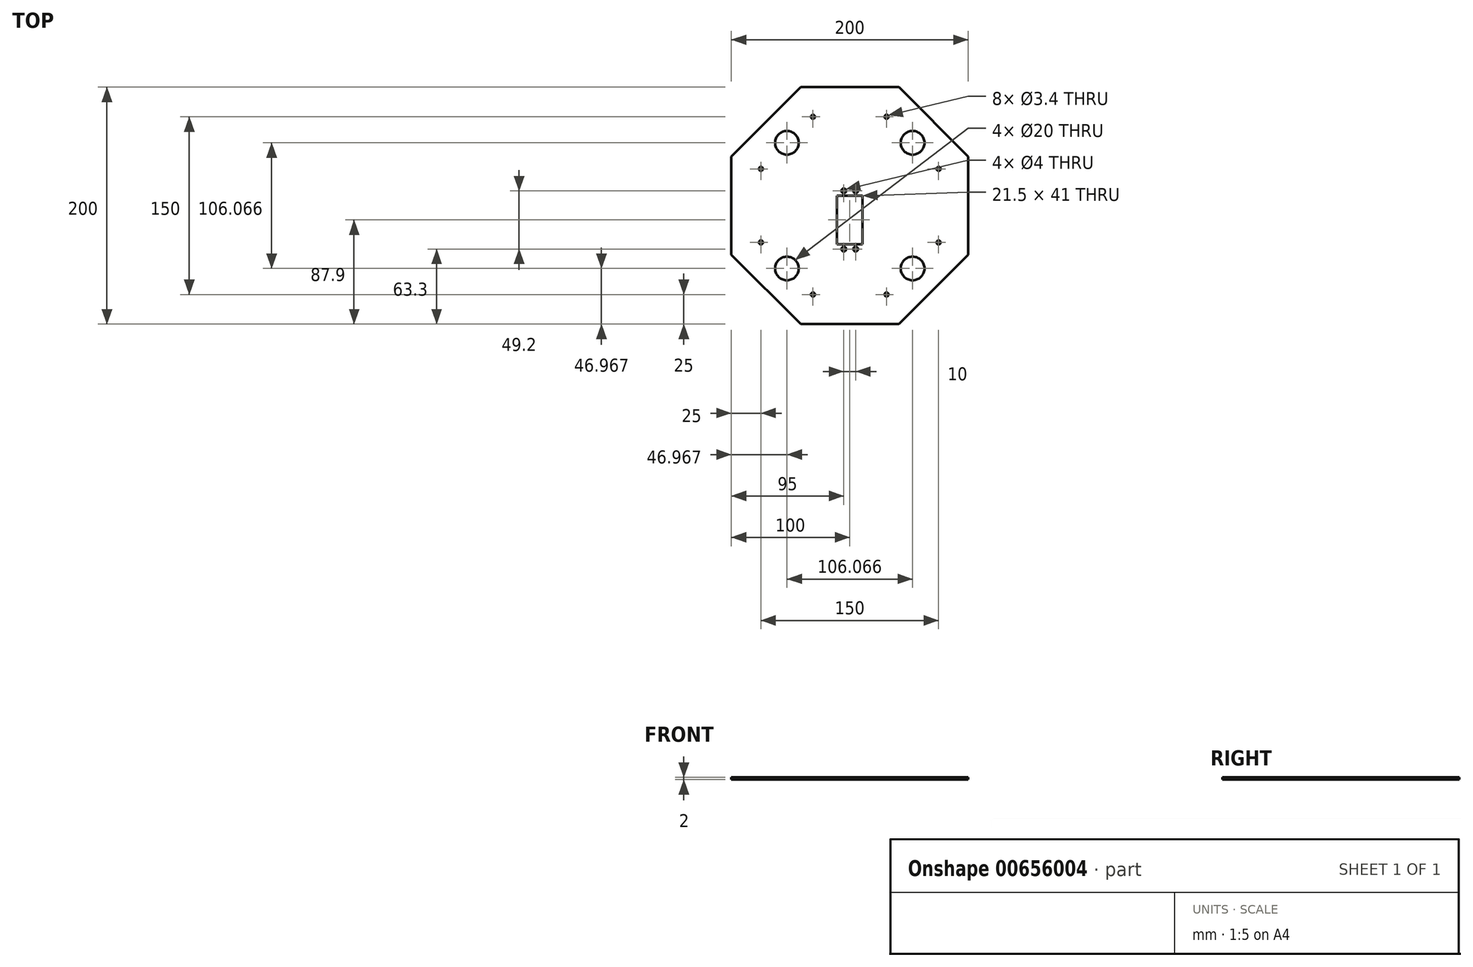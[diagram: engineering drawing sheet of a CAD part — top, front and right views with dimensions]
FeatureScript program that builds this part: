
annotation { "Feature Type Name" : "Feature", "Feature Type Description" : "" }
export const myFeature = defineFeature(function(context is Context, id is Id, definition is map)
    precondition{}
    {
        {
            var Q0;
            Q0=qCreatedBy(makeId("Top.planeOp"),FACE);
            var sketch = newSketch(context, id + "F0", { "sketchPlane" : qUnion([Q0])});
            skLineSegment(sketch, "E0.bottom", {"start": v(-10.75, 8.4) * mm, "end": v(10.75, 8.4) * mm});
            skLineSegment(sketch, "E0.top", {"start": v(-10.75, -32.6) * mm, "end": v(10.75, -32.6) * mm});
            skLineSegment(sketch, "E0.left", {"start": v(-10.75, 8.4) * mm, "end": v(-10.75, -32.6) * mm});
            skLineSegment(sketch, "E0.right", {"start": v(10.75, 8.4) * mm, "end": v(10.75, -32.6) * mm});
            skCircle(sketch, "E1", {"center": v(-5, 12.5) * mm, "radius": 2 * mm});
            skCircle(sketch, "E2", {"center": v(5, 12.5) * mm, "radius": 2 * mm});
            skCircle(sketch, "E3", {"center": v(-5, -36.7) * mm, "radius": 2 * mm});
            skCircle(sketch, "E4", {"center": v(5, -36.7) * mm, "radius": 2 * mm});
            skCircle(sketch, "E5", {"center": v(-53.03, 53.03) * mm, "radius": 10 * mm});
            skCircle(sketch, "E6", {"center": v(53.03, 53.03) * mm, "radius": 10 * mm});
            skCircle(sketch, "E7", {"center": v(-53.03, -53.03) * mm, "radius": 10 * mm});
            skCircle(sketch, "E8", {"center": v(53.03, -53.03) * mm, "radius": 10 * mm});
            skPoint(sketch, "E9.middle", {"position": v(0, 0) * mm});
            skPoint(sketch, "E10", {"position": v(0, -12.1) * mm});
            skLineSegment(sketch, "E11.0", {"start": v(-41.42, 100) * mm, "end": v(41.42, 100) * mm});
            skLineSegment(sketch, "E11.1", {"start": v(41.42, 100) * mm, "end": v(100, 41.42) * mm});
            skLineSegment(sketch, "E11.2", {"start": v(100, 41.42) * mm, "end": v(100, -41.42) * mm});
            skLineSegment(sketch, "E11.3", {"start": v(100, -41.42) * mm, "end": v(41.42, -100) * mm});
            skLineSegment(sketch, "E11.4", {"start": v(41.42, -100) * mm, "end": v(-41.42, -100) * mm});
            skLineSegment(sketch, "E11.5", {"start": v(-41.42, -100) * mm, "end": v(-100, -41.42) * mm});
            skLineSegment(sketch, "E11.6", {"start": v(-100, -41.42) * mm, "end": v(-100, 41.42) * mm});
            skLineSegment(sketch, "E11.7", {"start": v(-100, 41.42) * mm, "end": v(-41.42, 100) * mm});
            skPoint(sketch, "E12.0.midPoint", {"position": v(0, 75) * mm});
            skCircle(sketch, "E13", {"center": v(-31.07, 75) * mm, "radius": 1.7 * mm});
            skCircle(sketch, "E14", {"center": v(31.07, 75) * mm, "radius": 1.7 * mm});
            skCircle(sketch, "E15", {"center": v(75, 31.07) * mm, "radius": 1.7 * mm});
            skCircle(sketch, "E16", {"center": v(75, -31.07) * mm, "radius": 1.7 * mm});
            skCircle(sketch, "E17", {"center": v(31.07, -75) * mm, "radius": 1.7 * mm});
            skCircle(sketch, "E18", {"center": v(-31.07, -75) * mm, "radius": 1.7 * mm});
            skCircle(sketch, "E19", {"center": v(-75, -31.07) * mm, "radius": 1.7 * mm});
            skCircle(sketch, "E20", {"center": v(-75, 31.07) * mm, "radius": 1.7 * mm});
            skSolve(sketch);
        }
        {
            var Q0;
            Q0=makeQuery(id+"F0.imprint","IMPRINT",FACE,{"disambiguationData":[TD([[makeQuery(id+"F0.imprint","IMPRINT",EDGE,{"derivedFrom":sQuery(id+"F0.wireOp",EDGE,"E0.bottom")}),1.0]])]});
            extrude(context, id + "F1", {"entities" : qUnion([Q0]), "depth" : 2 * mm, "offsetDistance" : 25 * mm});
        }
    });
